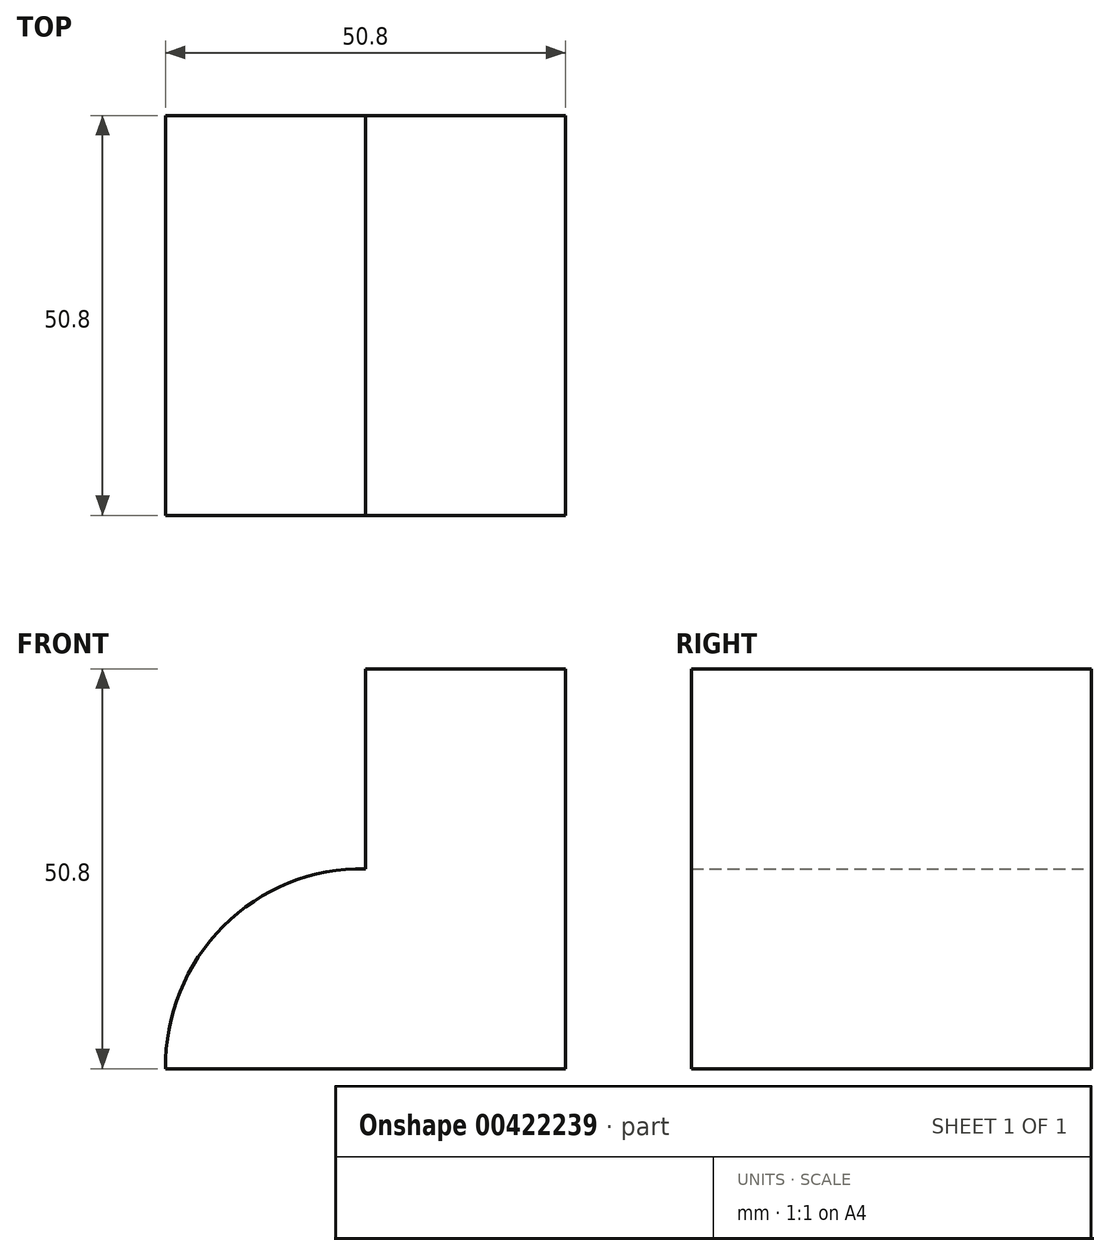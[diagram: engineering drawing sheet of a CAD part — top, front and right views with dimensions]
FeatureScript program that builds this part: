
annotation { "Feature Type Name" : "Feature", "Feature Type Description" : "" }
export const myFeature = defineFeature(function(context is Context, id is Id, definition is map)
    precondition{}
    {
        {
            var Q0;
            Q0=qCreatedBy(makeId("Front.planeOp"),FACE);
            var sketch = newSketch(context, id + "F0", { "sketchPlane" : qUnion([Q0])});
            skLineSegment(sketch, "E0", {"start": v(0, 0) * mm, "end": v(-50.8, 0) * mm});
            skLineSegment(sketch, "E1", {"start": v(0, 0) * mm, "end": v(0, 50.8) * mm});
            skLineSegment(sketch, "E2", {"start": v(0, 50.8) * mm, "end": v(-25.4, 50.8) * mm});
            skLineSegment(sketch, "E3", {"start": v(-25.4, 50.8) * mm, "end": v(-25.4, 25.4) * mm});
            skArc(sketch, "E4", {"start": v(-25.4, 25.4) * mm, "mid": v(-43.48, 18.08) * mm, "end": v(-50.8, 0) * mm});
            skSolve(sketch);
        }
        {
            var Q0;
            Q0 = qSketchRegion(id + "F0", true);
            extrude(context, id + "F1", {"entities" : qUnion([Q0]), "depth" : 50.8 * mm});
        }
    });
